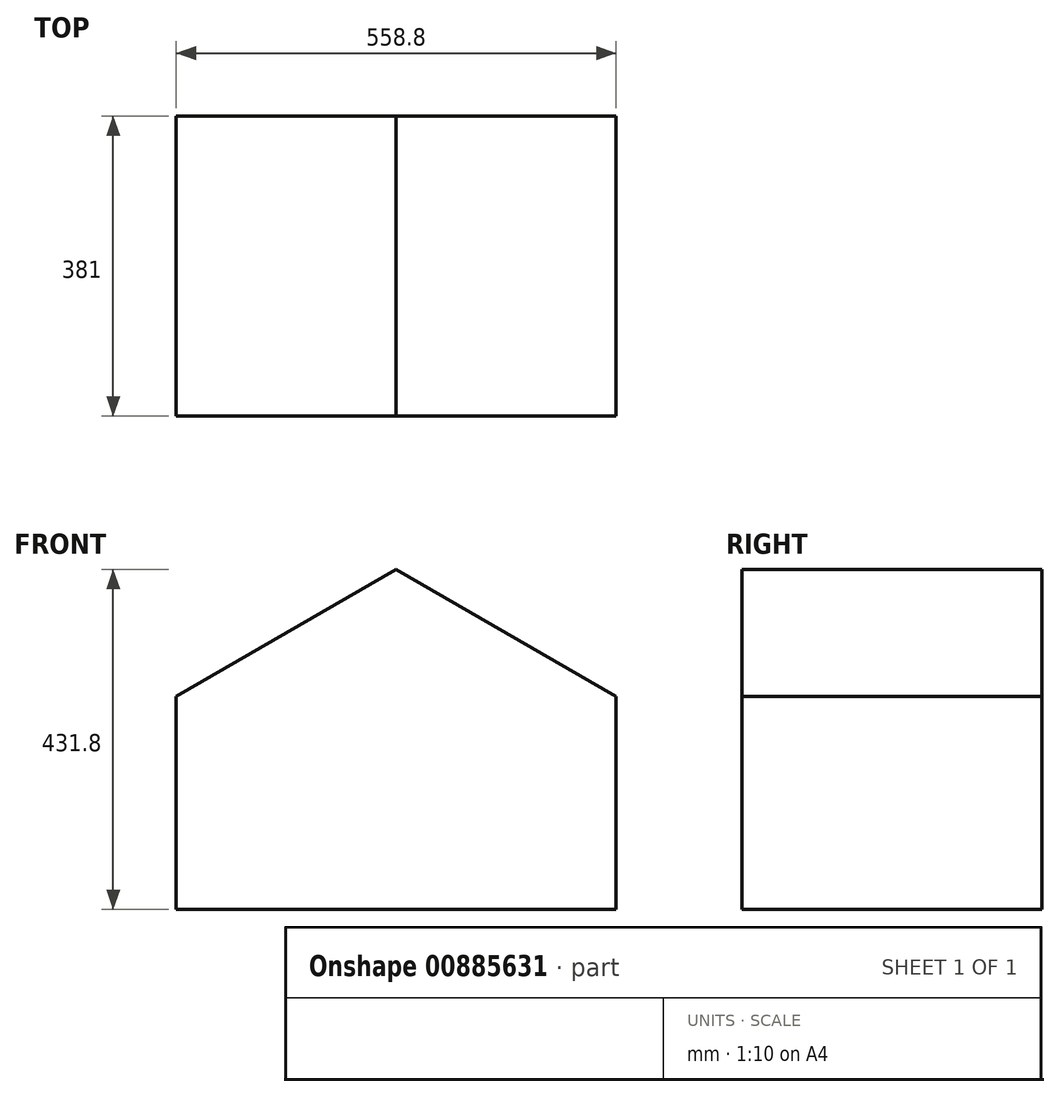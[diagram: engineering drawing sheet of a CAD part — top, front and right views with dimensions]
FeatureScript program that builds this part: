
annotation { "Feature Type Name" : "Feature", "Feature Type Description" : "" }
export const myFeature = defineFeature(function(context is Context, id is Id, definition is map)
    precondition{}
    {
        {
            var Q0;
            Q0=qCreatedBy(makeId("Front.planeOp"),FACE);
            var sketch = newSketch(context, id + "F0", { "sketchPlane" : qUnion([Q0])});
            skLineSegment(sketch, "E0.top", {"start": v(-279.4, -215.9) * mm, "end": v(279.4, -215.9) * mm});
            skLineSegment(sketch, "E0.left", {"start": v(-279.4, 54.68) * mm, "end": v(-279.4, -215.9) * mm});
            skLineSegment(sketch, "E0.right", {"start": v(279.4, 54.68) * mm, "end": v(279.4, -215.9) * mm});
            skPoint(sketch, "E0.middle", {"position": v(0, 0) * mm});
            skLineSegment(sketch, "E1", {"start": v(0, 215.9) * mm, "end": v(279.4, 54.68) * mm});
            skLineSegment(sketch, "E2", {"start": v(0, 215.9) * mm, "end": v(-279.4, 54.68) * mm});
            skPoint(sketch, "E3.orphan", {"position": v(279.4, 215.9) * mm});
            skPoint(sketch, "E4.orphan", {"position": v(-279.4, 215.9) * mm});
            skSolve(sketch);
        }
        {
            var Q0;
            Q0=makeQuery(id+"FKfTRDOmo9uQaw9_0.opExtrude","CAP_FACE",FACE,{"disambiguationData":[OSD([sQuery(id+"F0.wireOp",EDGE,"E0.bottom"),sQuery(id+"F0.wireOp",EDGE,"E0.top"),sQuery(id+"F0.wireOp",EDGE,"E0.left"),sQuery(id+"F0.wireOp",EDGE,"E0.right")])],"isStart":true});
            var sketch = newSketch(context, id + "F1", { "sketchPlane" : qUnion([Q0])});
            skSolve(sketch);
        }
        {
            var Q0;
            Q0=makeQuery(id+"F0.imprint","IMPRINT",FACE,{"disambiguationData":[TD([[makeQuery(id+"F0.imprint","IMPRINT",EDGE,{"derivedFrom":sQuery(id+"F0.wireOp",EDGE,"E0.top")}),1.0]])]});
            extrude(context, id + "F2", {"entities" : qUnion([Q0]), "depth" : 381 * mm, "offsetDistance" : 25.4 * mm});
        }
        {
            var Q0;
            Q0=makeQuery(id+"F2.opExtrude","CAP_FACE",FACE,{"disambiguationData":[OSD([sQuery(id+"F0.wireOp",EDGE,"E0.top"),sQuery(id+"F0.wireOp",EDGE,"E0.left"),sQuery(id+"F0.wireOp",EDGE,"E0.right"),sQuery(id+"F0.wireOp",EDGE,"E1"),sQuery(id+"F0.wireOp",EDGE,"E2")])],"isStart":true});
            var sketch = newSketch(context, id + "F3", { "sketchPlane" : qUnion([Q0])});
            skCircle(sketch, "E5", {"center": v(0, -25.4) * mm, "radius": 76.2 * mm});
            skCircle(sketch, "E6", {"center": v(0, -25.4) * mm, "radius": 158.75 * mm});
            skPoint(sketch, "E7.start.orphan", {"position": v(0, 50.8) * mm});
            skPoint(sketch, "E8.start.orphan", {"position": v(0, -215.9) * mm});
            skSolve(sketch);
        }
        {
            var Q0;
            Q0=sQuery(id+"F3.wireOp",EDGE,"E5");
            var Q1;
            Q1=sQuery(id+"F3.wireOp",EDGE,"E6");
            extrude(context, id + "F4", {"bodyType" : ToolBodyType.SURFACE, "surfaceEntities" : qUnion([Q0, Q1]), "depth" : 165.1 * mm, "offsetDistance" : 25.4 * mm});
        }
    });
